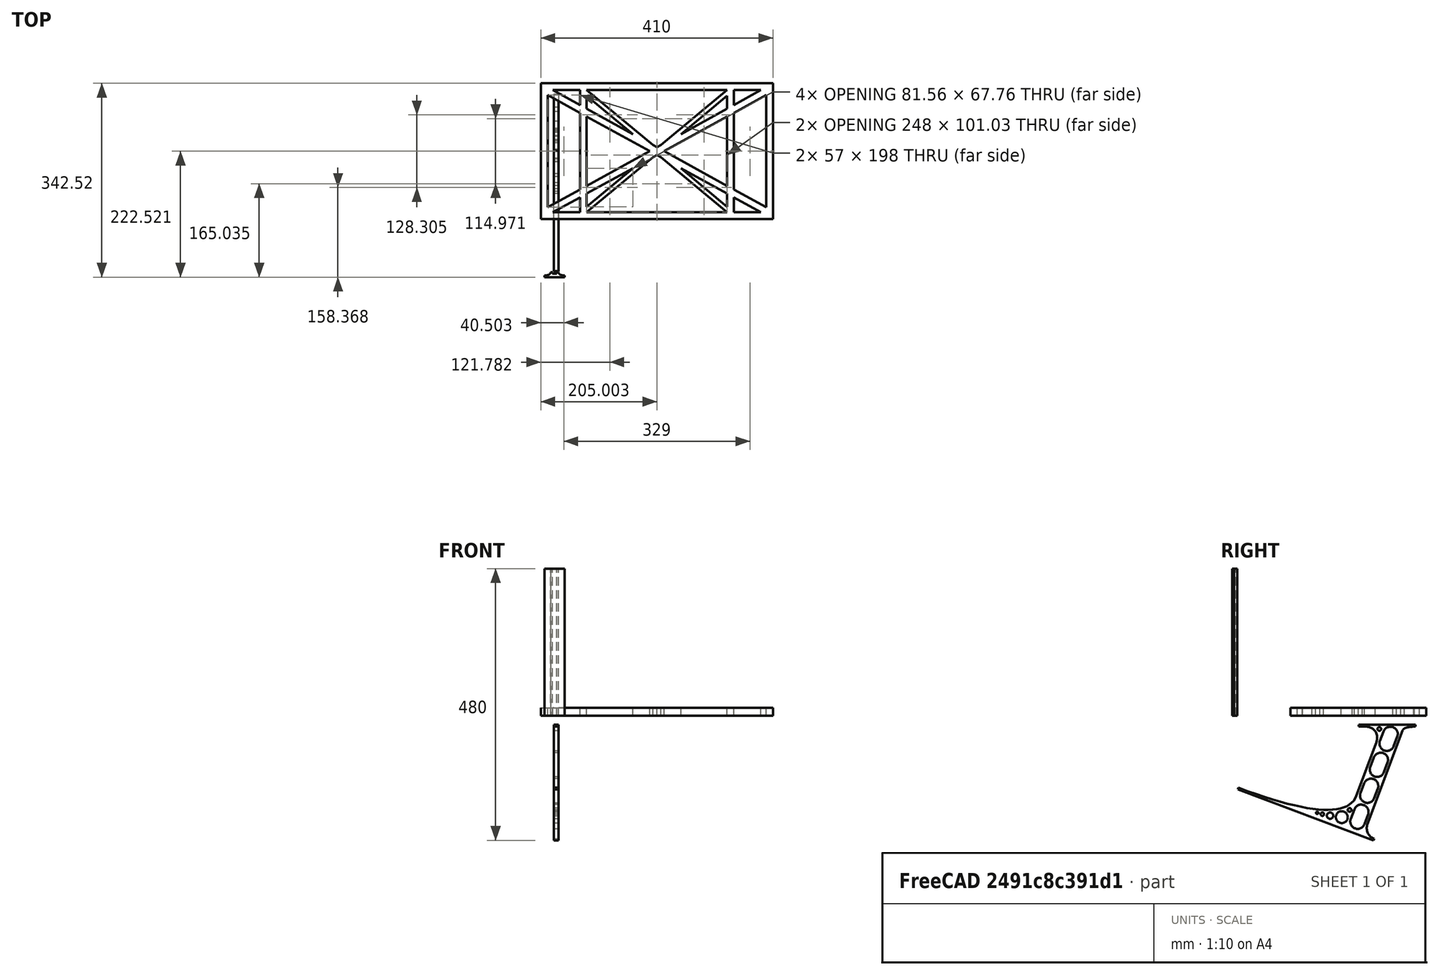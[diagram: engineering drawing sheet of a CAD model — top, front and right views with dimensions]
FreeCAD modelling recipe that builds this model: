
FCSTD DOCUMENT  (FreeCAD 0.19R0.19.2)
Label: laptopStand045
License: All rights reserved
LicenseURL: http://en.wikipedia.org/wiki/All_rights_reserved
objects: Sketcher::SketchObject×3, Part::Extrusion×3
note: 6 computed .brp shape members not serialized (recipe doc carries the construction recipe); baked Part::Feature solids carry a one-line shape summary decoded from their .brp

FEATURE [Sketcher::SketchObject] Sketch
  FullyConstrained = false
  sketch-geometry (69):
    g0: LineSegment StartX=-22.9272 StartY=136.221 StartZ=0 EndX=387.073 EndY=136.221 EndZ=0
    g1: LineSegment StartX=-22.9272 StartY=-103.779 StartZ=0 EndX=387.073 EndY=-103.779 EndZ=0
    g2: LineSegment StartX=375.073 StartY=115.221 StartZ=0 EndX=318.073 EndY=83.9235 EndZ=0
    g3: LineSegment StartX=-10.9272 StartY=-82.7794 StartZ=0 EndX=46.0728 EndY=-51.4823 EndZ=0
    g4: LineSegment StartX=-1.92719 StartY=124.221 StartZ=0 EndX=46.0728 EndY=97.8651 EndZ=0
    g5: LineSegment StartX=366.073 StartY=-91.7794 StartZ=0 EndX=318.073 EndY=-65.424 EndZ=0
    g6: LineSegment StartX=-10.9272 StartY=115.221 StartZ=0 EndX=-10.9272 EndY=-82.7794 EndZ=0
    g7: LineSegment StartX=375.073 StartY=-82.7794 StartZ=0 EndX=375.073 EndY=115.221 EndZ=0
    g8: LineSegment StartX=-1.92719 StartY=-91.7794 StartZ=0 EndX=46.0728 EndY=-91.7794 EndZ=0
    g9: LineSegment StartX=318.073 StartY=124.221 StartZ=0 EndX=366.073 EndY=124.221 EndZ=0
    g10: LineSegment StartX=306.073 StartY=-81.8102 StartZ=0 EndX=224.513 EndY=-14.0532 EndZ=0
    g11: LineSegment StartX=58.0728 StartY=114.251 StartZ=0 EndX=139.632 EndY=46.4944 EndZ=0
    g12: LineSegment StartX=306.073 StartY=124.221 StartZ=0 EndX=189.124 EndY=27.0628 EndZ=0
    g13: LineSegment StartX=58.0728 StartY=-91.7794 StartZ=0 EndX=175.022 EndY=5.37834 EndZ=0
    g14: LineSegment StartX=46.0728 StartY=124.221 StartZ=0 EndX=46.0728 EndY=97.8651 EndZ=0
    g15: LineSegment StartX=58.0728 StartY=-81.8102 StartZ=0 EndX=58.0728 EndY=-58.8351 EndZ=0
    g16: LineSegment StartX=318.073 StartY=124.221 StartZ=0 EndX=318.073 EndY=97.8651 EndZ=0
    g17: LineSegment StartX=306.073 StartY=114.251 StartZ=0 EndX=306.073 EndY=91.2763 EndZ=0
    g18: LineSegment StartX=224.513 StartY=46.4944 StartZ=0 EndX=306.073 EndY=114.251 EndZ=0
    g19: LineSegment StartX=175.022 StartY=27.0628 StartZ=0 EndX=58.0728 EndY=124.221 EndZ=0
    g20: LineSegment StartX=169.377 StartY=16.2206 StartZ=0 EndX=58.0728 EndY=77.3346 EndZ=0
    g21: LineSegment StartX=139.632 StartY=-14.0532 StartZ=0 EndX=58.0728 EndY=-81.8102 EndZ=0
    g22: LineSegment StartX=194.768 StartY=16.2206 StartZ=0 EndX=306.073 EndY=-44.8935 EndZ=0
    g23: LineSegment StartX=224.513 StartY=46.4944 StartZ=0 EndX=306.073 EndY=91.2763 EndZ=0
    g24: LineSegment StartX=175.022 StartY=27.0628 StartZ=0 EndX=179.022 EndY=24.8665 EndZ=0
    g25: LineSegment StartX=139.632 StartY=-14.0532 StartZ=0 EndX=58.0728 EndY=-58.8351 EndZ=0
    g26: LineSegment StartX=189.124 StartY=5.37834 StartZ=0 EndX=185.124 EndY=7.57463 EndZ=0
    g27: LineSegment StartX=189.124 StartY=5.37834 StartZ=0 EndX=306.073 EndY=-91.7794 EndZ=0
    g28: LineSegment StartX=306.073 StartY=77.3346 StartZ=0 EndX=306.073 EndY=-44.8935 EndZ=0
    g29: LineSegment StartX=318.073 StartY=83.9235 StartZ=0 EndX=318.073 EndY=-51.4823 EndZ=0
    g30: LineSegment StartX=318.073 StartY=97.8651 StartZ=0 EndX=366.073 EndY=124.221 EndZ=0
    g31: LineSegment StartX=306.073 StartY=77.3346 StartZ=0 EndX=194.768 EndY=16.2206 EndZ=0
    g32: LineSegment StartX=306.073 StartY=-58.8351 StartZ=0 EndX=224.513 EndY=-14.0532 EndZ=0
    g33: LineSegment StartX=306.073 StartY=-58.8351 StartZ=0 EndX=306.073 EndY=-81.8102 EndZ=0
    g34: LineSegment StartX=318.073 StartY=-51.4823 StartZ=0 EndX=375.073 EndY=-82.7794 EndZ=0
    g35: LineSegment StartX=318.073 StartY=-65.424 StartZ=0 EndX=318.073 EndY=-91.7794 EndZ=0
    g36: LineSegment StartX=306.073 StartY=124.221 StartZ=0 EndX=58.0728 EndY=124.221 EndZ=0
    g37: LineSegment StartX=318.073 StartY=-91.7794 StartZ=0 EndX=366.073 EndY=-91.7794 EndZ=0
    g38: LineSegment StartX=58.0728 StartY=-91.7794 StartZ=0 EndX=306.073 EndY=-91.7794 EndZ=0
    g39: LineSegment StartX=58.0728 StartY=-44.8935 StartZ=0 EndX=58.0728 EndY=77.3346 EndZ=0
    g40: LineSegment StartX=46.0728 StartY=-65.424 StartZ=0 EndX=-1.92719 EndY=-91.7794 EndZ=0
    g41: LineSegment StartX=46.0728 StartY=-65.424 StartZ=0 EndX=46.0728 EndY=-91.7794 EndZ=0
    g42: LineSegment StartX=58.0728 StartY=-44.8935 StartZ=0 EndX=169.377 EndY=16.2206 EndZ=0
    g43: LineSegment StartX=58.0728 StartY=91.2763 StartZ=0 EndX=58.0728 EndY=114.251 EndZ=0
    g44: LineSegment StartX=46.0728 StartY=83.9235 StartZ=0 EndX=46.0728 EndY=-51.4823 EndZ=0
    g45: LineSegment StartX=46.0728 StartY=124.221 StartZ=0 EndX=-1.92719 EndY=124.221 EndZ=0
    g46: LineSegment StartX=58.0728 StartY=91.2763 StartZ=0 EndX=139.632 EndY=46.4944 EndZ=0
    g47: LineSegment StartX=46.0728 StartY=83.9235 StartZ=0 EndX=-10.9272 EndY=115.221 EndZ=0
    g48: LineSegment StartX=-22.9272 StartY=136.221 StartZ=0 EndX=-42.9272 EndY=136.221 EndZ=0
    g49: LineSegment StartX=387.073 StartY=136.221 StartZ=0 EndX=407.073 EndY=136.221 EndZ=0
    g50: LineSegment StartX=-42.9272 StartY=136.221 StartZ=0 EndX=-42.9272 EndY=-103.779 EndZ=0
    g51: LineSegment StartX=-22.9272 StartY=-103.779 StartZ=0 EndX=-42.9272 EndY=-103.779 EndZ=0
    g52: LineSegment StartX=407.073 StartY=136.221 StartZ=0 EndX=407.073 EndY=-103.779 EndZ=0
    g53: LineSegment StartX=387.073 StartY=-103.779 StartZ=0 EndX=407.073 EndY=-103.779 EndZ=0
    g54: LineSegment StartX=179.022 StartY=27.0628 StartZ=0 EndX=179.022 EndY=124.221 EndZ=0
    g55: LineSegment StartX=185.124 StartY=27.0628 StartZ=0 EndX=185.124 EndY=124.221 EndZ=0
    g56: LineSegment StartX=179.022 StartY=27.0628 StartZ=0 EndX=179.022 EndY=24.8665 EndZ=0
    g57: LineSegment StartX=185.124 StartY=27.0628 StartZ=0 EndX=185.124 EndY=24.8665 EndZ=0
    g58: LineSegment StartX=185.124 StartY=7.57463 StartZ=0 EndX=185.124 EndY=-91.7794 EndZ=0
    g59: LineSegment StartX=179.022 StartY=7.57463 StartZ=0 EndX=179.022 EndY=-91.7794 EndZ=0
    g60: LineSegment StartX=189.124 StartY=27.0628 StartZ=0 EndX=185.124 EndY=24.8665 EndZ=0
    g61: LineSegment StartX=175.022 StartY=5.37834 StartZ=0 EndX=179.022 EndY=7.57463 EndZ=0
    g62: ArcOfCircle CenterX=-129.442 CenterY=22.1087 CenterZ=0 NormalX=0 NormalY=0 NormalZ=1 AngleXU=0 Radius=8 StartAngle=1e-16 EndAngle=3.14159
    g63: ArcOfCircle CenterX=-129.442 CenterY=-87.8913 CenterZ=0 NormalX=0 NormalY=0 NormalZ=1 AngleXU=0 Radius=8 StartAngle=3.14159 EndAngle=6.28319
    g64: LineSegment StartX=-137.442 StartY=22.1087 StartZ=0 EndX=-137.442 EndY=-87.8913 EndZ=0
    g65: LineSegment StartX=-121.442 StartY=22.1087 StartZ=0 EndX=-121.442 EndY=-87.8913 EndZ=0
    g66: LineSegment StartX=-137.442 StartY=22.1087 StartZ=0 EndX=-121.442 EndY=22.1087 EndZ=0
    g67: LineSegment StartX=-129.442 StartY=-87.8913 StartZ=0 EndX=-129.442 EndY=22.1087 EndZ=0
    g68: LineSegment StartX=-1.92718 StartY=-91.7794 StartZ=0 EndX=-42.9272 EndY=-91.7794 EndZ=0
  constraints (140):
    c: Horizontal(g0)
    c: Distance(g0) = 410
    c: Horizontal(g1)
    c: Block(g0)
    c: Horizontal(g8)
    c: Horizontal(g9)
    c: PointOnObject(g31,g4)
    c: Tangent(g5,g20)
    c: PointOnObject(g20,g3)
    c: PointOnObject(g22,g2)
    c: Coincident(g46,g11)
    c: Coincident(g24,g19)
    c: Coincident(g18,g23)
    c: Coincident(g25,g21)
    c: Coincident(g32,g10)
    c: Coincident(g27,g26)
    c: Coincident(g18,g17)
    c: Tangent(g17,g28)
    c: Tangent(g16,g29)
    c: Coincident(g23,g17)
    c: Tangent(g23,g30)
    c: Coincident(g2,g29)
    c: Coincident(g31,g28)
    c: Tangent(g2,g31)
    c: Coincident(g33,g10)
    c: Tangent(g5,g32)
    c: Tangent(g28,g33)
    c: Coincident(g22,g28)
    c: Tangent(g22,g34)
    c: Coincident(g29,g34)
    c: Coincident(g35,g5)
    c: Tangent(g29,g35)
    c: Coincident(g21,g15)
    c: Tangent(g15,g39)
    c: Coincident(g25,g15)
    c: Tangent(g25,g40)
    c: Coincident(g41,g40)
    c: Tangent(g14,g41)
    c: Coincident(g3,g44)
    c: Coincident(g42,g39)
    c: Tangent(g3,g42)
    c: Tangent(g39,g43)
    c: Tangent(g14,g44)
    c: Coincident(g11,g43)
    c: PointOnObject(g36,g19)
    c: Tangent(g36,g45)
    c: Coincident(g4,g14)
    c: Coincident(g46,g43)
    c: Tangent(g4,g46)
    c: Coincident(g20,g39)
    c: Coincident(g47,g44)
    c: Tangent(g20,g47)
    c: Block(g19)
    c: Block(g12)
    c: Block(g36)
    c: Block(g16)
    c: Block(g30)
    c: Block(g2)
    c: Block(g34)
    c: Block(g7)
    c: Block(g32)
    c: Block(g33)
    c: Block(g5)
    c: Block(g35)
    c: Block(g18)
    c: Block(g27)
    c: Block(g38)
    c: Block(g13)
    c: Block(g25)
    c: Block(g21)
    c: Block(g41)
    c: Block(g40)
    c: Block(g3)
    c: Block(g6)
    c: Block(g47)
    c: Block(g4)
    c: Block(g14)
    c: Block(g11)
    c: Block(g43)
    c: Block(g31)
    c: Block(g28)
    c: Block(g20)
    c: Block(g42)
    c: Block(g45)
    c: Block(g9)
    c: Block(g37)
    c: Block(g8)
    c: Horizontal(g48)
    c: Distance(g48) = 20
    c: Coincident(g49,g0)
    c: Horizontal(g49)
    c: Distance(g49) = 20
    c: Coincident(g50,g48)
    c: Vertical(g50)
    c: Horizontal(g51)
    c: Coincident(g51,g50)
    c: Coincident(g52,g49)
    c: Vertical(g52)
    c: Coincident(g53,g1)
    c: Horizontal(g53)
    c: Coincident(g53,g52)
    c: Block(g52)
    c: Block(g51)
    c: Block(g50)
    c: Block(g1)
    c: Vertical(g54)
    c: Vertical(g55)
    c: Vertical(g56)
    c: Vertical(g57)
    c: PointOnObject(g55,g36)
    c: PointOnObject(g54,g36)
    c: Tangent(g57,g58)
    c: PointOnObject(g58,g38)
    c: PointOnObject(g59,g38)
    c: Tangent(g56,g59)
    c: Coincident(g24,g56)
    c: Coincident(g26,g58)
    c: Block(g54)
    c: Block(g55)
    c: Block(g59)
    c: Block(g58)
    c: Coincident(g60,g12)
    c: Coincident(g60,g57)
    c: Coincident(g61,g13)
    c: Coincident(g61,g59)
    c: Tangent(g62,g65) = 1.5708
    c: Tangent(g62,g64) = -1.5708
    c: Tangent(g64,g63) = -1.5708
    c: Tangent(g65,g63) = 1.5708
    c: Vertical(g64)
    c: Equal(g62,g63)
    c: Coincident(g66,g62)
    c: Coincident(g66,g62)
    c: Distance(g66) = 16
    c: Coincident(g67,g63)
    c: Coincident(g67,g62)
    c: Distance(g67) = 110
    c: Coincident(g68,g8)
    c: Horizontal(g68)
    c: PointOnObject(g68,g50)
FEATURE [Sketcher::SketchObject] Sketch001
  FullyConstrained = true
  MapMode = 4
  Placement = pos=(0,0,0) rot=(0.57735,0.57735,0.57735;2.0944rad)
  Support = -> [Sketch]
  sketch-geometry (46):
    g0: BSplineCurve PolesCount=3 KnotsCount=2 Degree=2 IsPeriodic=0
    g1: ArcOfCircle CenterX=73.122 CenterY=-32.2909 CenterZ=0 NormalX=0 NormalY=0 NormalZ=1 AngleXU=0 Radius=13 StartAngle=5.92268 EndAngle=9.06428
    g2: ArcOfCircle CenterX=66.7816 CenterY=-49.1439 CenterZ=0 NormalX=0 NormalY=0 NormalZ=1 AngleXU=0 Radius=13 StartAngle=2.78068 EndAngle=5.92131
    g3: ArcOfCircle CenterX=55.9263 CenterY=-78.1807 CenterZ=0 NormalX=0 NormalY=0 NormalZ=1 AngleXU=0 Radius=13 StartAngle=5.92268 EndAngle=9.06428
    g4: ArcOfCircle CenterX=49.5884 CenterY=-95.0342 CenterZ=0 NormalX=0 NormalY=0 NormalZ=1 AngleXU=0 Radius=13 StartAngle=2.78068 EndAngle=5.92131
    g5: ArcOfCircle CenterX=38.7206 CenterY=-124.067 CenterZ=0 NormalX=0 NormalY=0 NormalZ=1 AngleXU=0 Radius=13 StartAngle=5.92268 EndAngle=9.06428
    g6: ArcOfCircle CenterX=32.3875 CenterY=-140.92 CenterZ=0 NormalX=0 NormalY=0 NormalZ=1 AngleXU=0 Radius=13 StartAngle=2.78068 EndAngle=5.92131
    g7: ArcOfCircle CenterX=21.4715 CenterY=-169.934 CenterZ=0 NormalX=0 NormalY=0 NormalZ=1 AngleXU=0 Radius=13 StartAngle=5.92268 EndAngle=9.06428
    g8: ArcOfCircle CenterX=15.1336 CenterY=-186.787 CenterZ=0 NormalX=0 NormalY=0 NormalZ=1 AngleXU=0 Radius=13 StartAngle=2.78068 EndAngle=5.92131
    g9-g12: Circle x4 (B-spline internal-alignment scaffolding for g13; pole/knot coordinates omitted)
    g13: BSplineCurve PolesCount=4 KnotsCount=2 Degree=3 IsPeriodic=0
    g14: GeomPoint X=28.8094 Y=-19.0875 Z=0
    g15: GeomPoint X=47.0443 Y=-50.4712 Z=0
    g16: Circle CenterX=53.5586 CenterY=-23.2695 CenterZ=0 NormalX=0 NormalY=0 NormalZ=1 AngleXU=0 Radius=3.24518
    g17: Circle CenterX=-195.441 CenterY=-127.082 CenterZ=0 NormalX=0 NormalY=0 NormalZ=1 AngleXU=0 Radius=1
    g18: Circle CenterX=-8.24091 CenterY=-197.481 CenterZ=0 NormalX=0 NormalY=0 NormalZ=1 AngleXU=0 Radius=1
    g19: Circle CenterX=12.8789 CenterY=-141.321 CenterZ=0 NormalX=0 NormalY=0 NormalZ=1 AngleXU=0 Radius=1
    g20: BSplineCurve PolesCount=3 KnotsCount=2 Degree=2 IsPeriodic=0
    g21: GeomPoint X=-195.441 Y=-127.082 Z=0
    g22: GeomPoint X=12.8789 Y=-141.321 Z=0
    g23: Circle CenterX=-12.8016 CenterY=-179.036 CenterZ=0 NormalX=0 NormalY=0 NormalZ=1 AngleXU=0 Radius=10.5072
    g24: Circle CenterX=0.933922 CenterY=-166.43 CenterZ=0 NormalX=0 NormalY=0 NormalZ=1 AngleXU=0 Radius=3.26661
    g25: Circle CenterX=-33.5518 CenterY=-176.44 CenterZ=0 NormalX=0 NormalY=0 NormalZ=1 AngleXU=0 Radius=5.64388
    g26: Circle CenterX=-47.2366 CenterY=-173.859 CenterZ=0 NormalX=0 NormalY=0 NormalZ=1 AngleXU=0 Radius=3.01653
    g27: Circle CenterX=-56.2595 CenterY=-171.456 CenterZ=0 NormalX=0 NormalY=0 NormalZ=1 AngleXU=0 Radius=2.12826
    g28: ArcOfCircle CenterX=51.2151 CenterY=-198.473 CenterZ=0 NormalX=0 NormalY=0 NormalZ=1 AngleXU=0 Radius=20 StartAngle=2.78189 EndAngle=4.35269
    g29: LineSegment StartX=32.4951 StartY=-191.433 StartZ=0 EndX=94.6577 EndY=-26.1351 EndZ=0
    g30: LineSegment StartX=43.1192 StartY=-220.001 StartZ=0 EndX=-196.497 EndY=-129.89 EndZ=0
    g31: LineSegment StartX=43.1192 StartY=-220.001 StartZ=0 EndX=44.1752 EndY=-217.193 EndZ=0
    g32: LineSegment StartX=117.223 StartY=-19.0875 StartZ=0 EndX=117.223 EndY=-16.0875 EndZ=0
    g33: LineSegment StartX=117.223 StartY=-16.0875 StartZ=0 EndX=17.2232 EndY=-16.0875 EndZ=0
    g34: LineSegment StartX=17.2232 StartY=-16.0875 StartZ=0 EndX=17.2232 EndY=-19.0875 EndZ=0
    g35: LineSegment StartX=28.8094 StartY=-19.0875 StartZ=0 EndX=17.2232 EndY=-19.0875 EndZ=0
    g36: LineSegment StartX=47.0443 StartY=-50.4712 StartZ=0 EndX=12.8789 EndY=-141.321 EndZ=0
    g37: LineSegment StartX=-195.441 StartY=-127.082 StartZ=0 EndX=-196.497 EndY=-129.89 EndZ=0
    g38: LineSegment StartX=85.2864 StartY=-36.8765 StartZ=0 EndX=78.9396 EndY=-53.7463 EndZ=0
    g39: LineSegment StartX=60.9577 StartY=-27.7052 StartZ=0 EndX=54.6191 EndY=-44.5532 EndZ=0
    g40: LineSegment StartX=68.0907 StartY=-82.7664 StartZ=0 EndX=61.7465 EndY=-99.6365 EndZ=0
    g41: LineSegment StartX=43.7619 StartY=-73.595 StartZ=0 EndX=37.426 EndY=-90.4435 EndZ=0
    g42: LineSegment StartX=50.885 StartY=-128.652 StartZ=0 EndX=44.5456 EndY=-145.522 EndZ=0
    g43: LineSegment StartX=26.5562 StartY=-119.481 StartZ=0 EndX=20.2251 EndY=-136.329 EndZ=0
    g44: LineSegment StartX=9.3071 StartY=-165.349 StartZ=0 EndX=2.97115 EndY=-182.197 EndZ=0
    g45: LineSegment StartX=33.6358 StartY=-174.52 StartZ=0 EndX=27.2917 EndY=-191.39 EndZ=0
  constraints (70):
    c: Block(g0)
    c: Block(g1)
    c: Block(g2)
    c: Block(g4)
    c: Block(g3)
    c: Block(g6)
    c: Block(g5)
    c: Block(g8)
    c: Block(g7)
    c: Weight(g9) = 1
    c: Equal(g9,g10)
    c: Equal(g9,g11)
    c: Equal(g9,g12)
    c: InternalAlignment(g9-g12 -> g13) x4
    c: InternalAlignment(g14,g13)
    c: InternalAlignment(g15,g13)
    c: Block(g16)
    c: Weight(g17) = 1
    c: Equal(g17,g18)
    c: Equal(g17,g19)
    c: InternalAlignment(g17,g20)
    c: InternalAlignment(g18,g20)
    c: InternalAlignment(g19,g20)
    c: InternalAlignment(g21,g20)
    c: InternalAlignment(g22,g20)
    c: Block(g20)
    c: Block(g23)
    c: Block(g24)
    c: Block(g25)
    c: Block(g26)
    c: Block(g27)
    c: Block(g28)
    c: Coincident(g29,g28)
    c: Coincident(g29,g0)
    c: Block(g13)
    c: Coincident(g31,g30)
    c: Coincident(g31,g28)
    c: Block(g31)
    c: Coincident(g32,g0)
    c: Vertical(g32)
    c: Coincident(g33,g32)
    c: Horizontal(g33)
    c: Coincident(g34,g33)
    c: Vertical(g34)
    c: Block(g33)
    c: Coincident(g35,g13)
    c: Coincident(g35,g34)
    c: Horizontal(g35)
    c: Coincident(g36,g13)
    c: Coincident(g36,g20)
    c: Coincident(g37,g20)
    c: Coincident(g37,g30)
    c: Block(g30)
    c: Coincident(g38,g1)
    c: Coincident(g38,g2)
    c: Coincident(g39,g1)
    c: Coincident(g39,g2)
    c: Coincident(g40,g3)
    c: Coincident(g40,g4)
    c: Coincident(g41,g3)
    c: Coincident(g41,g4)
    c: Coincident(g42,g5)
    c: Coincident(g42,g6)
    c: Coincident(g43,g5)
    c: Coincident(g43,g6)
    c: Coincident(g44,g7)
    c: Coincident(g44,g8)
    c: Coincident(g45,g7)
    c: Coincident(g45,g8)
    c: Distance(g30) = 256
FEATURE [Part::Extrusion] Extrude002
  Base = -> Sketch001
  Dir = (1,0,0)
  DirMode = 2
  FaceMakerClass = Part::FaceMakerBullseye
  LengthFwd = 8
  LengthRev = 0
  Solid = true
  Symmetric = false
FEATURE [Sketcher::SketchObject] Sketch002
  FullyConstrained = true
  sketch-geometry (20):
    g0: LineSegment StartX=-2.77179 StartY=-200.304 StartZ=0 EndX=5.22821 EndY=-200.304 EndZ=0
    g1: LineSegment StartX=5.22821 StartY=-200.304 StartZ=0 EndX=5.22821 EndY=-197.304 EndZ=0
    g2: LineSegment StartX=-2.77179 StartY=-200.304 StartZ=0 EndX=-2.77179 EndY=-197.304 EndZ=0
    g3: LineSegment StartX=5.22821 StartY=-197.304 StartZ=0 EndX=8.22821 EndY=-197.304 EndZ=0
    g4: LineSegment StartX=-2.77179 StartY=-197.304 StartZ=0 EndX=-5.77179 EndY=-197.304 EndZ=0
    g5: LineSegment StartX=19.2282 StartY=-203.304 StartZ=0 EndX=19.2282 EndY=-206.304 EndZ=0
    g6: LineSegment StartX=-16.7718 StartY=-203.304 StartZ=0 EndX=-16.7718 EndY=-206.304 EndZ=0
    g7: LineSegment StartX=-16.7718 StartY=-206.304 StartZ=0 EndX=19.2282 EndY=-206.304 EndZ=0
    g8: Circle CenterX=-16.7718 CenterY=-203.304 CenterZ=0 NormalX=0 NormalY=0 NormalZ=1 AngleXU=0 Radius=1
    g9: Circle CenterX=-5.77179 CenterY=-203.304 CenterZ=0 NormalX=0 NormalY=0 NormalZ=1 AngleXU=0 Radius=1
    g10: Circle CenterX=-5.77179 CenterY=-197.304 CenterZ=0 NormalX=0 NormalY=0 NormalZ=1 AngleXU=0 Radius=1
    g11: BSplineCurve PolesCount=3 KnotsCount=2 Degree=2 IsPeriodic=0
    g12: GeomPoint X=-16.7718 Y=-203.304 Z=0
    g13: GeomPoint X=-5.77179 Y=-197.304 Z=0
    g14: Circle CenterX=19.2282 CenterY=-203.304 CenterZ=0 NormalX=0 NormalY=0 NormalZ=1 AngleXU=0 Radius=1
    g15: Circle CenterX=8.22821 CenterY=-203.304 CenterZ=0 NormalX=0 NormalY=0 NormalZ=1 AngleXU=0 Radius=1
    g16: Circle CenterX=8.22821 CenterY=-197.304 CenterZ=0 NormalX=0 NormalY=0 NormalZ=1 AngleXU=0 Radius=1
    g17: BSplineCurve PolesCount=3 KnotsCount=2 Degree=2 IsPeriodic=0
    g18: GeomPoint X=19.2282 Y=-203.304 Z=0
    g19: GeomPoint X=8.22821 Y=-197.304 Z=0
  constraints (41):
    c: Horizontal(g0)
    c: Distance(g0) = 8
    c: Coincident(g1,g0)
    c: Vertical(g1)
    c: Distance(g1) = 3
    c: Coincident(g2,g0)
    c: Vertical(g2)
    c: Distance(g2) = 3
    c: Coincident(g3,g1)
    c: Horizontal(g3)
    c: Distance(g3) = 3
    c: Coincident(g4,g2)
    c: Horizontal(g4)
    c: Distance(g4) = 3
    c: Vertical(g5)
    c: Vertical(g6)
    c: Coincident(g7,g6)
    c: Coincident(g7,g5)
    c: Weight(g8) = 1
    c: Equal(g8,g9)
    c: Equal(g8,g10)
    c: Coincident(g11,g4)
    c: InternalAlignment(g8,g11)
    c: InternalAlignment(g9,g11)
    c: InternalAlignment(g10,g11)
    c: InternalAlignment(g12,g11)
    c: InternalAlignment(g13,g11)
    c: Coincident(g17,g5)
    c: Weight(g14) = 1
    c: Equal(g14,g15)
    c: Equal(g14,g16)
    c: Coincident(g17,g3)
    c: InternalAlignment(g14,g17)
    c: InternalAlignment(g15,g17)
    c: InternalAlignment(g16,g17)
    c: InternalAlignment(g18,g17)
    c: InternalAlignment(g19,g17)
    c: Block(g7)
    c: Block(g17)
    c: Block(g11)
    c: Block(g6)
FEATURE [Part::Extrusion] Extrude003
  Base = -> Sketch002
  Dir = (0,0,1)
  DirMode = 2
  FaceMakerClass = Part::FaceMakerBullseye
  LengthFwd = 260
  LengthRev = 0
  Solid = true
  Symmetric = false
FEATURE [Part::Extrusion] Extrude
  Base = -> Sketch
  Dir = (0,0,1)
  DirMode = 2
  FaceMakerClass = Part::FaceMakerBullseye
  LengthFwd = 14
  LengthRev = 0
  Solid = true
  Symmetric = false
